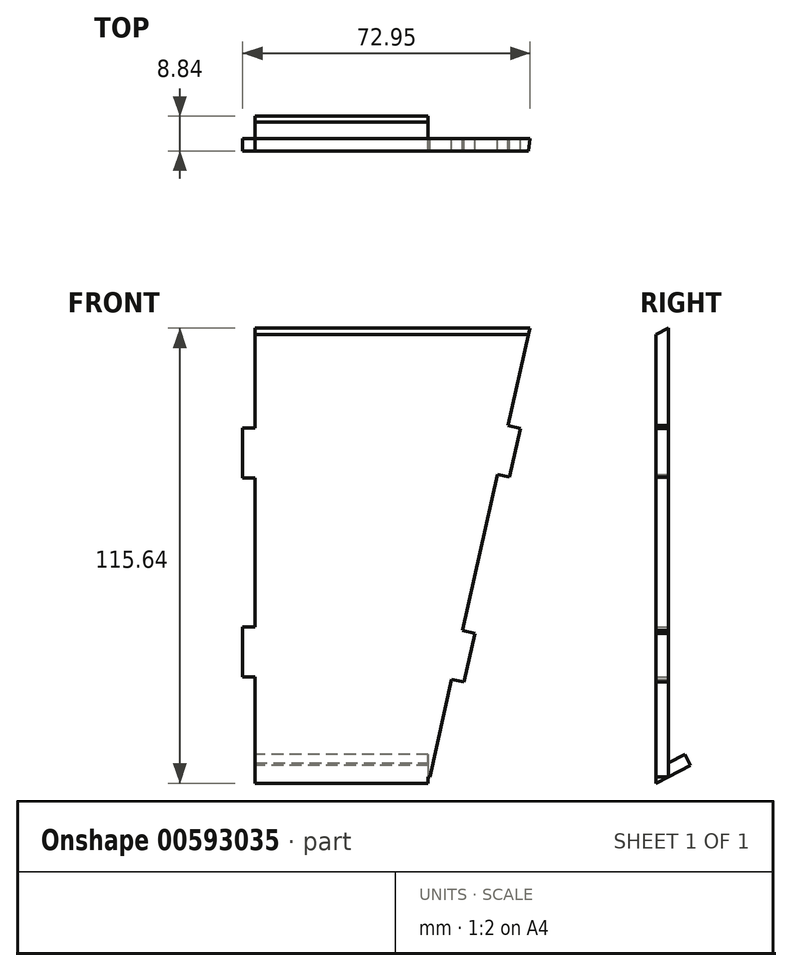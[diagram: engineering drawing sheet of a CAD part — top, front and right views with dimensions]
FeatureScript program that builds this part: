
annotation { "Feature Type Name" : "Feature", "Feature Type Description" : "" }
export const myFeature = defineFeature(function(context is Context, id is Id, definition is map)
    precondition{}
    {
        {
            var Q0;
            Q0=qCreatedBy(makeId("Front.planeOp"),FACE);
            var sketch = newSketch(context, id + "F0", { "sketchPlane" : qUnion([Q0])});
            skLineSegment(sketch, "E0.bottom", {"start": v(9.45, -57.01) * mm, "end": v(-34.92, -57.01) * mm});
            skLineSegment(sketch, "E0.top", {"start": v(34.85, 57.01) * mm, "end": v(-34.92, 57.01) * mm});
            skLineSegment(sketch, "E0.right", {"start": v(-38.1, -31.61) * mm, "end": v(-38.1, -18.91) * mm});
            skPoint(sketch, "E0.middle", {"position": v(0, 0) * mm});
            skLineSegment(sketch, "E1", {"start": v(-34.92, -57.01) * mm, "end": v(9.45, -57.01) * mm});
            skLineSegment(sketch, "E2", {"start": v(18.07, -32.9) * mm, "end": v(20.83, -20.51) * mm});
            skPoint(sketch, "E3.orphan", {"position": v(38.1, -57.01) * mm});
            skLineSegment(sketch, "E4", {"start": v(-34.92, 57.01) * mm, "end": v(-34.92, 31.61) * mm});
            skLineSegment(sketch, "E5", {"start": v(-34.92, 31.61) * mm, "end": v(-38.1, 31.61) * mm});
            skLineSegment(sketch, "E6", {"start": v(-38.1, 31.61) * mm, "end": v(-38.1, 18.91) * mm});
            skLineSegment(sketch, "E7", {"start": v(-38.1, 18.91) * mm, "end": v(-34.93, 18.91) * mm});
            skLineSegment(sketch, "E8", {"start": v(-34.93, 18.91) * mm, "end": v(-34.92, -18.91) * mm});
            skLineSegment(sketch, "E9", {"start": v(-34.92, -18.91) * mm, "end": v(-38.1, -18.91) * mm});
            skLineSegment(sketch, "E10", {"start": v(-38.1, -18.91) * mm, "end": v(-38.1, -31.61) * mm});
            skLineSegment(sketch, "E11", {"start": v(-38.1, -31.61) * mm, "end": v(-34.92, -31.61) * mm});
            skLineSegment(sketch, "E12", {"start": v(-34.92, -31.61) * mm, "end": v(-34.92, -57.01) * mm});
            skPoint(sketch, "E13.orphan", {"position": v(-38.1, 57.01) * mm});
            skLineSegment(sketch, "E14.trimOffspring", {"start": v(-38.1, 18.91) * mm, "end": v(-38.1, 31.61) * mm});
            skPoint(sketch, "E15.orphan", {"position": v(-38.1, -57.01) * mm});
            skLineSegment(sketch, "E16", {"start": v(20.83, -20.51) * mm, "end": v(17.73, -19.82) * mm});
            skLineSegment(sketch, "E17", {"start": v(17.73, -19.82) * mm, "end": v(26.56, 19.82) * mm});
            skLineSegment(sketch, "E18", {"start": v(26.56, 19.82) * mm, "end": v(29.66, 19.13) * mm});
            skLineSegment(sketch, "E19", {"start": v(29.66, 19.13) * mm, "end": v(32.42, 31.53) * mm});
            skLineSegment(sketch, "E20", {"start": v(32.42, 31.53) * mm, "end": v(29.32, 32.22) * mm});
            skLineSegment(sketch, "E21", {"start": v(29.32, 32.22) * mm, "end": v(34.85, 57.01) * mm});
            skPoint(sketch, "E22.end.orphan", {"position": v(9.45, -57.01) * mm});
            skPoint(sketch, "E23.end.orphan", {"position": v(12.7, -42.4) * mm});
            skLineSegment(sketch, "E24", {"start": v(18.07, -32.9) * mm, "end": v(14.97, -32.22) * mm});
            skLineSegment(sketch, "E25", {"start": v(14.97, -32.22) * mm, "end": v(9.45, -57.01) * mm});
            skPoint(sketch, "E26.orphan", {"position": v(38.1, 57.01) * mm});
            skPoint(sketch, "E27.end.orphan", {"position": v(15.8, -43.1) * mm});
            skPoint(sketch, "E28.orphan", {"position": v(12.7, -57.01) * mm});
            skSolve(sketch);
        }
        {
            var Q0;
            Q0=qSketchRegion(id+"F0",true);
            extrude(context, id + "F1", {"entities" : qUnion([Q0]), "depth" : 3.17 * mm, "offsetDistance" : 25.4 * mm});
        }
        {
            var Q0;
            Q0=makeQuery(id+"F1.opExtrude","SWEPT_FACE",FACE,{"disambiguationData":[OSD([sQuery(id+"F0.wireOp",EDGE,"E12")])]});
            var sketch = newSketch(context, id + "F2", { "sketchPlane" : qUnion([Q0])});
            skLineSegment(sketch, "E29", {"start": v(0, -57.01) * mm, "end": v(-5.66, -54.13) * mm});
            skLineSegment(sketch, "E30", {"start": v(-5.66, -54.13) * mm, "end": v(-4.22, -51.3) * mm});
            skLineSegment(sketch, "E31", {"start": v(-4.22, -51.3) * mm, "end": v(3.18, -55.06) * mm});
            skLineSegment(sketch, "E32", {"start": v(3.18, -55.06) * mm, "end": v(3.18, -58.63) * mm});
            skLineSegment(sketch, "E33", {"start": v(0, -57.01) * mm, "end": v(3.18, -58.63) * mm});
            skSolve(sketch);
        }
        {
            var Q0;
            Q0=makeQuery(id+"F1.opExtrude","SWEPT_FACE",FACE,{"disambiguationData":[OSD([sQuery(id+"F0.wireOp",EDGE,"E4")])]});
            var sketch = newSketch(context, id + "F3", { "sketchPlane" : qUnion([Q0])});
            skLineSegment(sketch, "E34", {"start": v(0, 57.01) * mm, "end": v(3.18, 55.4) * mm});
            skLineSegment(sketch, "E35", {"start": v(3.18, 55.4) * mm, "end": v(3.18, 57.01) * mm});
            skLineSegment(sketch, "E36", {"start": v(3.18, 57.01) * mm, "end": v(0, 57.01) * mm});
            skSolve(sketch);
        }
        {
            var Q0;
            Q0=makeQuery(id+"F3.imprint","IMPRINT",FACE,{"disambiguationData":[TD([[makeQuery(id+"F3.imprint","IMPRINT",EDGE,{"derivedFrom":sQuery(id+"F3.wireOp",EDGE,"E34")}),1.0]])]});
            extrude(context, id + "F4", {"entities" : qUnion([Q0]), "operationType" : NewBodyOperationType.REMOVE, "oppositeDirection" : true, "depth" : 76.2 * mm, "offsetDistance" : 25.4 * mm});
        }
        {
            var Q0;
            Q0 = qSketchRegion(id + "F2", true);
            extrude(context, id + "F5", {"entities" : qUnion([Q0]), "operationType" : NewBodyOperationType.ADD, "oppositeDirection" : true, "depth" : 43.94 * mm, "offsetDistance" : 25.4 * mm});
        }
    });
